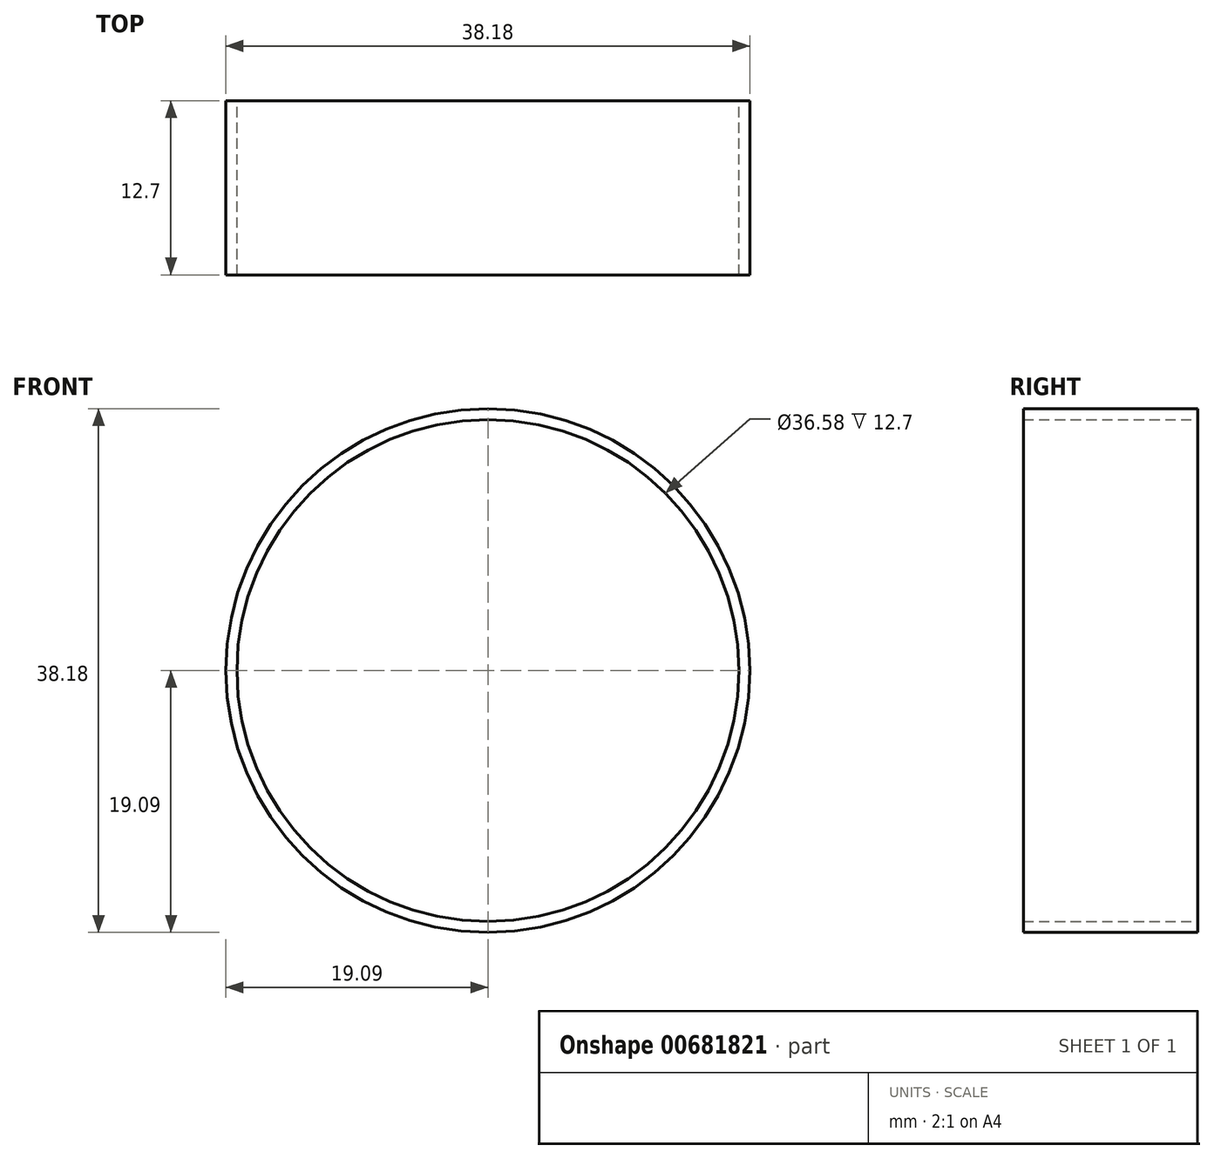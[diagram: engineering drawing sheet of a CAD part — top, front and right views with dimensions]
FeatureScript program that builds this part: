
annotation { "Feature Type Name" : "Feature", "Feature Type Description" : "" }
export const myFeature = defineFeature(function(context is Context, id is Id, definition is map)
    precondition{}
    {
        {
            var Q0;
            Q0=qCreatedBy(makeId("Front.planeOp"),FACE);
            var sketch = newSketch(context, id + "F0", { "sketchPlane" : qUnion([Q0])});
            skCircle(sketch, "E0", {"center": v(0, 0) * mm, "radius": 18.29 * mm});
            skCircle(sketch, "E1", {"center": v(0, 0) * mm, "radius": 19.09 * mm});
            skSolve(sketch);
        }
        {
            var Q0;
            Q0=makeQuery(id+"F0.imprint","IMPRINT",FACE,{"disambiguationData":[TD([[makeQuery(id+"F0.imprint","IMPRINT",EDGE,{"derivedFrom":sQuery(id+"F0.wireOp",EDGE,"E0")}),-1.0]])]});
            extrude(context, id + "F1", {"entities" : qUnion([Q0]), "depth" : 12.7 * mm, "offsetDistance" : 25.4 * mm});
        }
    });
